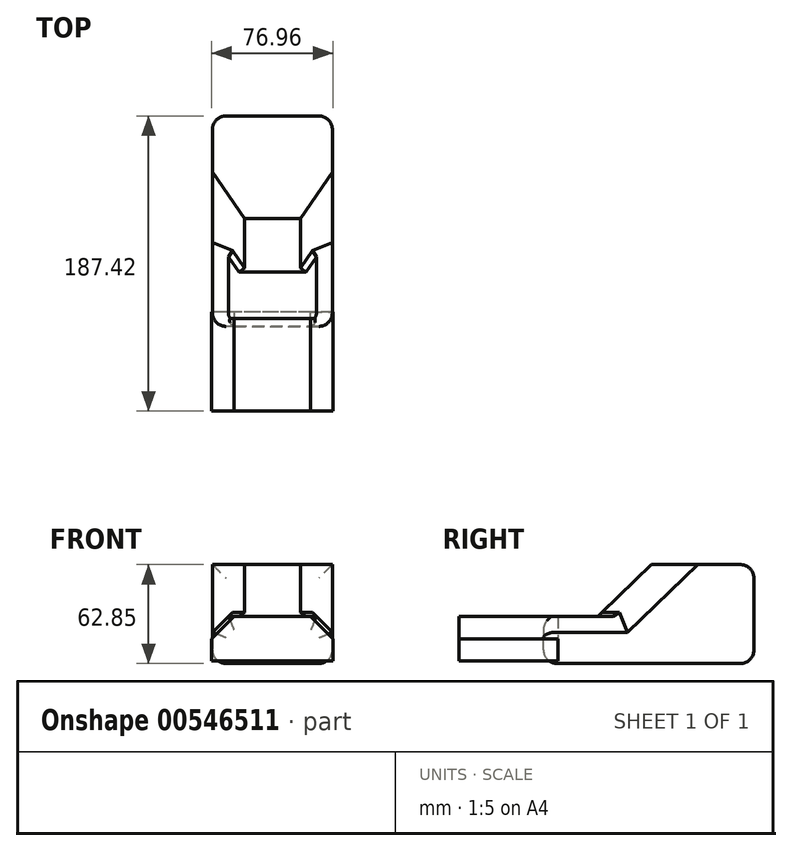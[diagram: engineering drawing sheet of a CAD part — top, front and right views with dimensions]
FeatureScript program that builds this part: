
annotation { "Feature Type Name" : "Feature", "Feature Type Description" : "" }
export const myFeature = defineFeature(function(context is Context, id is Id, definition is map)
    precondition{}
    {
        {
            var Q0;
            Q0=qCreatedBy(makeId("Right.planeOp"),FACE);
            var sketch = newSketch(context, id + "F0", { "sketchPlane" : qUnion([Q0])});
            skLineSegment(sketch, "E0", {"start": v(-34.46, -25.05) * mm, "end": v(0, -25.05) * mm});
            skLineSegment(sketch, "E1", {"start": v(0, -25.05) * mm, "end": v(34.16, 7.74) * mm});
            skLineSegment(sketch, "E2", {"start": v(34.16, 7.74) * mm, "end": v(99.14, 7.74) * mm});
            skLineSegment(sketch, "E3", {"start": v(99.14, 7.74) * mm, "end": v(99.14, -55.11) * mm});
            skLineSegment(sketch, "E4", {"start": v(99.14, -55.11) * mm, "end": v(-34.46, -55.11) * mm});
            skLineSegment(sketch, "E5", {"start": v(-34.46, -55.11) * mm, "end": v(-34.46, -25.05) * mm});
            skSolve(sketch);
        }
        {
            var Q0;
            Q0 = qSketchRegion(id + "F0", true);
            extrude(context, id + "F1", {"entities" : qUnion([Q0]), "depth" : 76.2 * mm, "offsetDistance" : 25.4 * mm});
        }
        {
            var Q0;
            Q0=makeQuery(id+"F1.opExtrude","CAP_EDGE",EDGE,{"disambiguationData":[OSD([sQuery(id+"F0.wireOp",EDGE,"E1")])],"isStart":false});
            var Q1;
            Q1=makeQuery(id+"F1.opExtrude","CAP_EDGE",EDGE,{"disambiguationData":[OSD([sQuery(id+"F0.wireOp",EDGE,"E1")])],"isStart":true});
            chamfer(context, id + "F2", {"entities" : qUnion([Q0, Q1]), "width" : 20.32 * mm, "tangentPropagation" : true});
        }
        {
            var Q0;
            Q0=makeQuery(id+"F1.opExtrude","CAP_EDGE",EDGE,{"disambiguationData":[OSD([sQuery(id+"F0.wireOp",EDGE,"E0")])],"isStart":false});
            var Q1;
            Q1=makeQuery(id+"F1.opExtrude","CAP_EDGE",EDGE,{"disambiguationData":[OSD([sQuery(id+"F0.wireOp",EDGE,"E0")])],"isStart":true});
            chamfer(context, id + "F3", {"entities" : qUnion([Q0, Q1]), "width" : 10.16 * mm, "tangentPropagation" : true});
        }
        {
            var Q0;
            Q0=makeQuery(id+"F2.opChamfer","BLEND_EDGE",EDGE,{"blendedFrom":[makeQuery(id+"F1.opExtrude","CAP_EDGE",EDGE,{"disambiguationData":[OSD([sQuery(id+"F0.wireOp",EDGE,"E1")])],"isStart":false}),makeQuery(id+"F1.opExtrude","SWEPT_FACE",FACE,{"disambiguationData":[OSD([sQuery(id+"F0.wireOp",EDGE,"E0")])]})],"blendedInto":[makeQuery(id+"F1.opExtrude","SWEPT_FACE",FACE,{"disambiguationData":[OSD([sQuery(id+"F0.wireOp",EDGE,"E0")])]})]});
            chamfer(context, id + "F4", {"entities" : qUnion([Q0]), "width" : 5.08 * mm, "tangentPropagation" : true});
        }
        {
            var Q0;
            Q0=makeQuery(id+"F2.opChamfer","BLEND_EDGE",EDGE,{"blendedFrom":[makeQuery(id+"F1.opExtrude","CAP_EDGE",EDGE,{"disambiguationData":[OSD([sQuery(id+"F0.wireOp",EDGE,"E1")])],"isStart":true}),makeQuery(id+"F1.opExtrude","SWEPT_FACE",FACE,{"disambiguationData":[OSD([sQuery(id+"F0.wireOp",EDGE,"E0")])]})],"blendedInto":[makeQuery(id+"F1.opExtrude","SWEPT_FACE",FACE,{"disambiguationData":[OSD([sQuery(id+"F0.wireOp",EDGE,"E0")])]})]});
            chamfer(context, id + "F5", {"entities" : qUnion([Q0]), "width" : 5.08 * mm, "tangentPropagation" : true});
        }
        {
            var Q0;
            Q0=makeQuery(id+"F1.opExtrude","SWEPT_EDGE",EDGE,{"disambiguationData":[OSD([sQuery(id+"F0.wireOp",EDGE,"E0"),sQuery(id+"F0.wireOp",EDGE,"E5")])]});
            chamfer(context, id + "F6", {"entities" : qUnion([Q0]), "width" : 5.08 * mm, "tangentPropagation" : true});
        }
        {
            var Q0;
            Q0=makeQuery(id+"F1.opExtrude","SWEPT_FACE",FACE,{"disambiguationData":[OSD([sQuery(id+"F0.wireOp",EDGE,"E5")])]});
            var Q1;
            Q1=makeQuery(id+"F1.opExtrude","SWEPT_FACE",FACE,{"disambiguationData":[OSD([sQuery(id+"F0.wireOp",EDGE,"E4")])]});
            var Q2;
            Q2=makeQuery(id+"F1.opExtrude","SWEPT_FACE",FACE,{"disambiguationData":[OSD([sQuery(id+"F0.wireOp",EDGE,"E3")])]});
            fillet(context, id + "F7", {"entities" : qUnion([Q0, Q1, Q2]), "radius" : 8.58 * mm, "tangentPropagation" : true, "allowEdgeOverflow" : false});
        }
        {
            var Q0;
            Q0=qCreatedBy(makeId("Right.planeOp"),FACE);
            var sketch = newSketch(context, id + "F8", { "sketchPlane" : qUnion([Q0])});
            skLineSegment(sketch, "E6.bottom", {"start": v(-25.39, -25.35) * mm, "end": v(-88.28, -25.35) * mm});
            skLineSegment(sketch, "E6.top", {"start": v(-25.39, -53.6) * mm, "end": v(-88.28, -53.6) * mm});
            skLineSegment(sketch, "E6.left", {"start": v(-25.39, -25.35) * mm, "end": v(-25.39, -53.6) * mm});
            skLineSegment(sketch, "E6.right", {"start": v(-88.28, -25.35) * mm, "end": v(-88.28, -53.6) * mm});
            skSolve(sketch);
        }
        {
            var Q0;
            Q0 = qSketchRegion(id + "F8", true);
            extrude(context, id + "F9", {"entities" : qUnion([Q0]), "depth" : 76.45 * mm, "offsetDistance" : 25.4 * mm, "hasSecondDirection" : true, "secondDirectionOppositeDirection" : true, "secondDirectionDepth" : 0.5 * mm});
        }
        {
            var Q0;
            Q0=makeQuery(id+"F9.opExtrude","CAP_EDGE",EDGE,{"disambiguationData":[OSD([sQuery(id+"F8.wireOp",EDGE,"E6.bottom")])],"isStart":false});
            var Q1;
            Q1=makeQuery(id+"F9.opExtrude","CAP_EDGE",EDGE,{"disambiguationData":[OSD([sQuery(id+"F8.wireOp",EDGE,"E6.bottom")])],"isStart":true});
            chamfer(context, id + "F10", {"entities" : qUnion([Q0, Q1]), "width" : 14.22 * mm, "tangentPropagation" : true});
        }
    });
